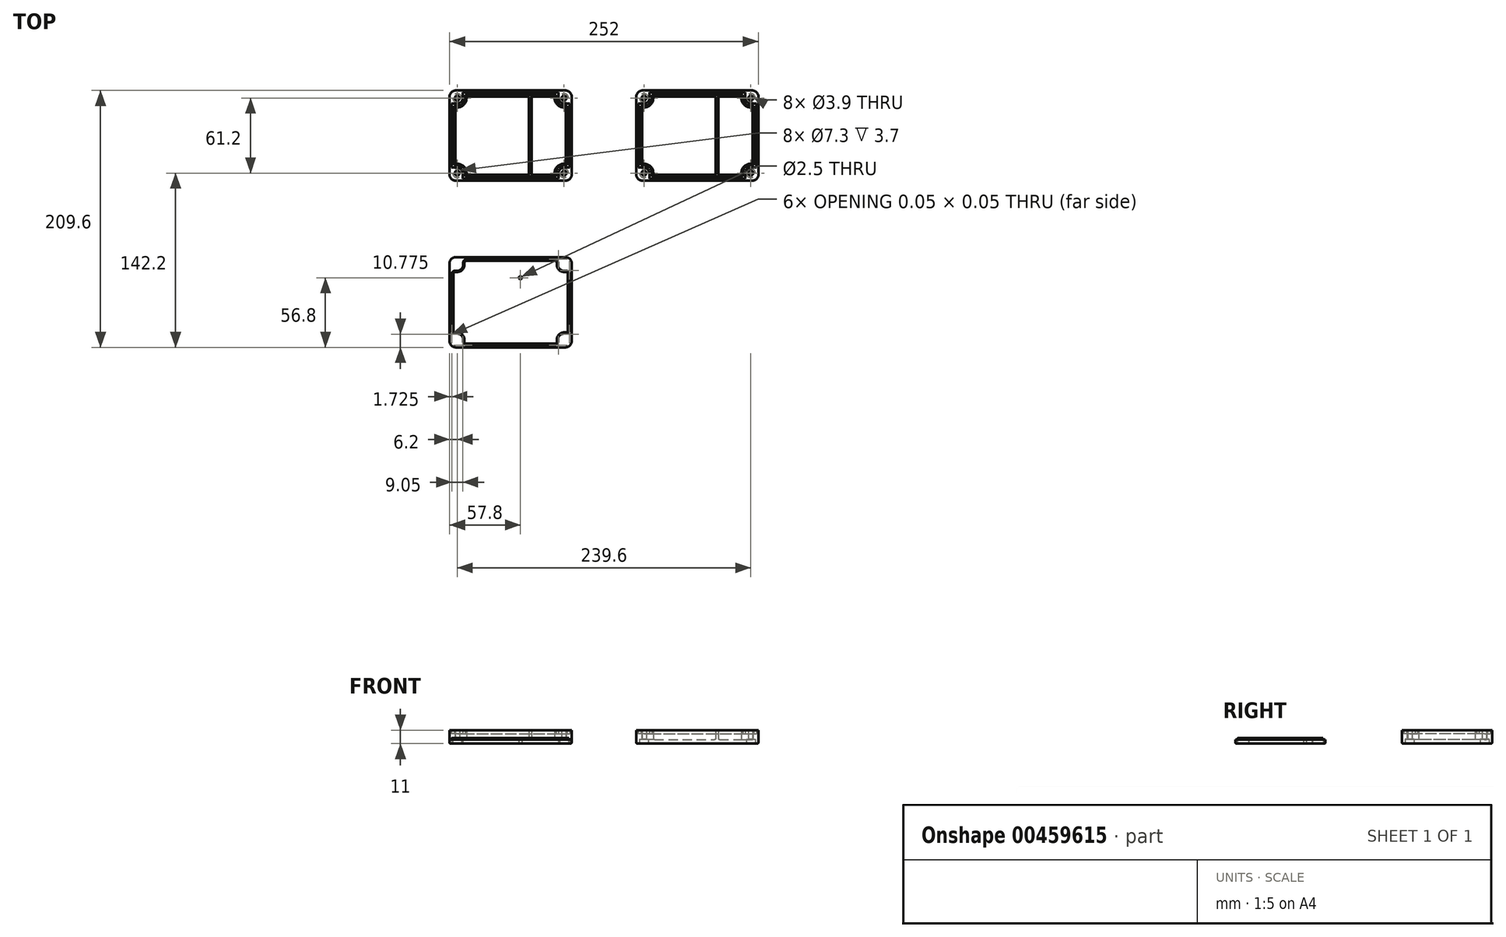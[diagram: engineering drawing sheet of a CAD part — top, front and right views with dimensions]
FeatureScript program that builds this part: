
annotation { "Feature Type Name" : "Feature", "Feature Type Description" : "" }
export const myFeature = defineFeature(function(context is Context, id is Id, definition is map)
    precondition{}
    {
        {
            var Q0;
            Q0=qCreatedBy(makeId("Top.planeOp"),FACE);
            var sketch = newSketch(context, id + "F0", { "sketchPlane" : qUnion([Q0])});
            skLineSegment(sketch, "E0.bottom", {"start": v(-25, 25) * mm, "end": v(25, 25) * mm, "construction": true});
            skLineSegment(sketch, "E0.top", {"start": v(-25, -25) * mm, "end": v(25, -25) * mm, "construction": true});
            skLineSegment(sketch, "E0.left", {"start": v(-25, 25) * mm, "end": v(-25, -25) * mm, "construction": true});
            skLineSegment(sketch, "E0.right", {"start": v(25, 25) * mm, "end": v(25, -25) * mm, "construction": true});
            skPoint(sketch, "E0.middle", {"position": v(0, 0) * mm});
            skLineSegment(sketch, "E1", {"start": v(-24, 32) * mm, "end": v(27, 32) * mm});
            skLineSegment(sketch, "E2", {"start": v(-33, 23) * mm, "end": v(-33, -23) * mm});
            skLineSegment(sketch, "E3", {"start": v(-24, -32) * mm, "end": v(27, -32) * mm});
            skLineSegment(sketch, "E4", {"start": v(28, 61.53) * mm, "end": v(28, -64.08) * mm, "construction": true});
            skLineSegment(sketch, "E5.bottom", {"start": v(31, 30) * mm, "end": v(47, 30) * mm, "construction": true});
            skLineSegment(sketch, "E5.top", {"start": v(31, -30) * mm, "end": v(47, -30) * mm, "construction": true});
            skLineSegment(sketch, "E5.left", {"start": v(31, 30) * mm, "end": v(31, -30) * mm, "construction": true});
            skLineSegment(sketch, "E5.right", {"start": v(47, 30) * mm, "end": v(47, -30) * mm, "construction": true});
            skPoint(sketch, "E5.middle", {"position": v(39, 0) * mm});
            skLineSegment(sketch, "E6", {"start": v(57, 23) * mm, "end": v(57, -23) * mm});
            skLineSegment(sketch, "E7", {"start": v(-32.8, 36.8) * mm, "end": v(56.8, 36.8) * mm});
            skLineSegment(sketch, "E8", {"start": v(-37.8, 31.8) * mm, "end": v(-37.8, -31.8) * mm});
            skLineSegment(sketch, "E9", {"start": v(-32.8, -36.8) * mm, "end": v(56.8, -36.8) * mm});
            skLineSegment(sketch, "E10", {"start": v(61.8, -31.8) * mm, "end": v(61.8, 31.8) * mm});
            skCircle(sketch, "E11", {"center": v(-31.6, 30.6) * mm, "radius": 1.95 * mm});
            skLineSegment(sketch, "E12.bottom", {"start": v(-25.1, 33.1) * mm, "end": v(49.1, 33.1) * mm});
            skLineSegment(sketch, "E12.top", {"start": v(-25.1, -33.1) * mm, "end": v(49.1, -33.1) * mm});
            skLineSegment(sketch, "E12.left", {"start": v(-34.1, 24.1) * mm, "end": v(-34.1, -24.1) * mm});
            skLineSegment(sketch, "E12.right", {"start": v(58.1, 24.1) * mm, "end": v(58.1, -24.1) * mm});
            skLineSegment(sketch, "E13.top", {"start": v(-27.1, -35.2) * mm, "end": v(51.1, -35.2) * mm});
            skLineSegment(sketch, "E13.right", {"start": v(60.2, 26.1) * mm, "end": v(60.2, -26.1) * mm});
            skLineSegment(sketch, "E14.trimOffspring", {"start": v(-27.1, 35.2) * mm, "end": v(51.1, 35.2) * mm});
            skLineSegment(sketch, "E15.trimOffspring", {"start": v(-36.2, 26.1) * mm, "end": v(-36.2, -26.1) * mm});
            skPoint(sketch, "E16.visualSharp", {"position": v(-37.8, 36.8) * mm});
            skArc(sketch, "E16.filletArc", {"start": v(-32.8, 36.8) * mm, "mid": v(-36.34, 35.34) * mm, "end": v(-37.8, 31.8) * mm});
            skLineSegment(sketch, "E17", {"start": v(27, 32) * mm, "end": v(27, -32) * mm});
            skLineSegment(sketch, "E18.MirrorCS", {"start": v(29, 32) * mm, "end": v(29, -32) * mm});
            skLineSegment(sketch, "E19.trimOffspring", {"start": v(29, 32) * mm, "end": v(48, 32) * mm});
            skLineSegment(sketch, "E20.trimOffspring", {"start": v(29, -32) * mm, "end": v(48, -32) * mm});
            skCircle(sketch, "E21", {"center": v(55.6, 30.6) * mm, "radius": 1.95 * mm});
            skArc(sketch, "E22", {"start": v(51.1, 30.6) * mm, "mid": v(52.42, 27.42) * mm, "end": v(55.6, 26.1) * mm});
            skArc(sketch, "E23", {"start": v(49.1, 30.6) * mm, "mid": v(51, 26) * mm, "end": v(55.6, 24.1) * mm});
            skArc(sketch, "E24", {"start": v(48, 30.6) * mm, "mid": v(50.23, 25.23) * mm, "end": v(55.6, 23) * mm});
            skCircle(sketch, "E25", {"center": v(55.6, -30.6) * mm, "radius": 1.95 * mm});
            skArc(sketch, "E26", {"start": v(55.6, -26.1) * mm, "mid": v(52.42, -27.42) * mm, "end": v(51.1, -30.6) * mm});
            skArc(sketch, "E27", {"start": v(55.6, -24.1) * mm, "mid": v(51, -26) * mm, "end": v(49.1, -30.6) * mm});
            skArc(sketch, "E28", {"start": v(55.6, -23) * mm, "mid": v(50.23, -25.23) * mm, "end": v(48, -30.6) * mm});
            skCircle(sketch, "E29", {"center": v(-31.6, -30.6) * mm, "radius": 1.95 * mm});
            skArc(sketch, "E30", {"start": v(-27.1, -30.6) * mm, "mid": v(-28.42, -27.42) * mm, "end": v(-31.6, -26.1) * mm});
            skArc(sketch, "E31", {"start": v(-25.1, -30.6) * mm, "mid": v(-27, -26) * mm, "end": v(-31.6, -24.1) * mm});
            skArc(sketch, "E32", {"start": v(-24, -30.6) * mm, "mid": v(-26.23, -25.23) * mm, "end": v(-31.6, -23) * mm});
            skLineSegment(sketch, "E33", {"start": v(48, 30.6) * mm, "end": v(48, 32) * mm});
            skLineSegment(sketch, "E34", {"start": v(49.1, 30.6) * mm, "end": v(49.1, 33.1) * mm});
            skLineSegment(sketch, "E35", {"start": v(51.1, 30.6) * mm, "end": v(51.1, 35.2) * mm});
            skLineSegment(sketch, "E36", {"start": v(55.6, 23) * mm, "end": v(57, 23) * mm});
            skLineSegment(sketch, "E37", {"start": v(55.6, 24.1) * mm, "end": v(58.1, 24.1) * mm});
            skLineSegment(sketch, "E38", {"start": v(55.6, 26.1) * mm, "end": v(60.2, 26.1) * mm});
            skLineSegment(sketch, "E39", {"start": v(55.6, -23) * mm, "end": v(57, -23) * mm});
            skLineSegment(sketch, "E40", {"start": v(55.6, -26.1) * mm, "end": v(60.2, -26.1) * mm});
            skLineSegment(sketch, "E41", {"start": v(48, -30.6) * mm, "end": v(48, -32) * mm});
            skLineSegment(sketch, "E42", {"start": v(49.1, -30.6) * mm, "end": v(49.1, -33.1) * mm});
            skLineSegment(sketch, "E43", {"start": v(51.1, -30.6) * mm, "end": v(51.1, -35.2) * mm});
            skLineSegment(sketch, "E44", {"start": v(55.6, -24.1) * mm, "end": v(58.1, -24.1) * mm});
            skArc(sketch, "E45", {"start": v(-31.6, 26.1) * mm, "mid": v(-28.42, 27.42) * mm, "end": v(-27.1, 30.6) * mm});
            skArc(sketch, "E46", {"start": v(-31.6, 24.1) * mm, "mid": v(-27, 26) * mm, "end": v(-25.1, 30.6) * mm});
            skArc(sketch, "E47", {"start": v(-31.6, 23) * mm, "mid": v(-26.23, 25.23) * mm, "end": v(-24, 30.6) * mm});
            skLineSegment(sketch, "E48", {"start": v(-24, 30.6) * mm, "end": v(-24, 32) * mm});
            skLineSegment(sketch, "E49", {"start": v(-25.1, 30.6) * mm, "end": v(-25.1, 33.1) * mm});
            skLineSegment(sketch, "E50", {"start": v(-27.1, 30.6) * mm, "end": v(-27.1, 35.2) * mm});
            skLineSegment(sketch, "E51", {"start": v(-31.6, 23) * mm, "end": v(-33, 23) * mm});
            skLineSegment(sketch, "E52", {"start": v(-31.6, 24.1) * mm, "end": v(-34.1, 24.1) * mm});
            skLineSegment(sketch, "E53", {"start": v(-31.6, 26.1) * mm, "end": v(-36.2, 26.1) * mm});
            skLineSegment(sketch, "E54", {"start": v(-24, -30.6) * mm, "end": v(-24, -32) * mm});
            skLineSegment(sketch, "E55", {"start": v(-25.1, -30.6) * mm, "end": v(-25.1, -33.1) * mm});
            skLineSegment(sketch, "E56", {"start": v(-27.1, -30.6) * mm, "end": v(-27.1, -35.2) * mm});
            skLineSegment(sketch, "E57", {"start": v(-31.6, -23) * mm, "end": v(-33, -23) * mm});
            skLineSegment(sketch, "E58", {"start": v(-31.6, -24.1) * mm, "end": v(-34.1, -24.1) * mm});
            skLineSegment(sketch, "E59", {"start": v(-31.6, -26.1) * mm, "end": v(-36.2, -26.1) * mm});
            skPoint(sketch, "E60.visualSharp", {"position": v(61.8, 36.8) * mm});
            skArc(sketch, "E60.filletArc", {"start": v(61.8, 31.8) * mm, "mid": v(60.34, 35.34) * mm, "end": v(56.8, 36.8) * mm});
            skPoint(sketch, "E61.visualSharp", {"position": v(61.8, -36.8) * mm});
            skArc(sketch, "E61.filletArc", {"start": v(56.8, -36.8) * mm, "mid": v(60.34, -35.34) * mm, "end": v(61.8, -31.8) * mm});
            skPoint(sketch, "E62.visualSharp", {"position": v(-37.8, -36.8) * mm});
            skArc(sketch, "E62.filletArc", {"start": v(-37.8, -31.8) * mm, "mid": v(-36.34, -35.34) * mm, "end": v(-32.8, -36.8) * mm});
            skSolve(sketch);
        }
        {
            var Q0;
            Q0=makeQuery(id+"F0.imprint","IMPRINT",FACE,{"disambiguationData":[TD([[makeQuery(id+"F0.imprint","IMPRINT",EDGE,{"derivedFrom":sQuery(id+"F0.wireOp",EDGE,"E7")}),-1.0]])]});
            var Q1;
            Q1=makeQuery(id+"F0.imprint","IMPRINT",FACE,{"disambiguationData":[TD([[makeQuery(id+"F0.imprint","IMPRINT",EDGE,{"derivedFrom":sQuery(id+"F0.wireOp",EDGE,"E1")}),1.0]])]});
            extrude(context, id + "F1", {"entities" : qUnion([Q0, Q1]), "depth" : 11 * mm});
        }
        {
            var Q0;
            Q0=makeQuery(id+"F0.imprint","IMPRINT",FACE,{"disambiguationData":[TD([[makeQuery(id+"F0.imprint","IMPRINT",EDGE,{"derivedFrom":sQuery(id+"F0.wireOp",EDGE,"E12.bottom")}),1.0]])]});
            extrude(context, id + "F2", {"entities" : qUnion([Q0]), "operationType" : NewBodyOperationType.ADD, "depth" : 8 * mm});
        }
        {
            var Q0;
            Q0=makeQuery(id+"F0.imprint","IMPRINT",FACE,{"disambiguationData":[TD([[makeQuery(id+"F0.imprint","IMPRINT",EDGE,{"derivedFrom":sQuery(id+"F0.wireOp",EDGE,"E6")}),-1.0]])]});
            var Q1;
            Q1=makeQuery(id+"F0.imprint","IMPRINT",FACE,{"disambiguationData":[TD([[makeQuery(id+"F0.imprint","IMPRINT",EDGE,{"derivedFrom":sQuery(id+"F0.wireOp",EDGE,"E1")}),-1.0]])]});
            extrude(context, id + "F3", {"entities" : qUnion([Q0, Q1]), "operationType" : NewBodyOperationType.ADD, "depth" : 3.2 * mm});
        }
        {
            var Q0;
            Q0=qCreatedBy(makeId("Top.planeOp"),FACE);
            var sketch = newSketch(context, id + "F4", { "sketchPlane" : qUnion([Q0])});
            skLineSegment(sketch, "E63", {"start": v(0, 0) * mm, "end": v(0, -187.5) * mm, "construction": true});
            skLineSegment(sketch, "E64", {"start": v(0, -136) * mm, "end": v(-72.43, -136) * mm, "construction": true});
            skLineSegment(sketch, "E65", {"start": v(0, -136) * mm, "end": v(90.36, -136) * mm, "construction": true});
            skLineSegment(sketch, "E66.bottom", {"start": v(-25, -111) * mm, "end": v(25, -111) * mm, "construction": true});
            skLineSegment(sketch, "E66.top", {"start": v(-25, -161) * mm, "end": v(25, -161) * mm, "construction": true});
            skLineSegment(sketch, "E66.left", {"start": v(-25, -111) * mm, "end": v(-25, -161) * mm, "construction": true});
            skLineSegment(sketch, "E66.right", {"start": v(25, -111) * mm, "end": v(25, -161) * mm, "construction": true});
            skPoint(sketch, "E66.middle", {"position": v(0, -136) * mm});
            skLineSegment(sketch, "E67.bottom", {"start": v(31, -106) * mm, "end": v(47, -106) * mm, "construction": true});
            skLineSegment(sketch, "E67.top", {"start": v(31, -166) * mm, "end": v(47, -166) * mm, "construction": true});
            skLineSegment(sketch, "E67.left", {"start": v(31, -106) * mm, "end": v(31, -166) * mm, "construction": true});
            skLineSegment(sketch, "E67.right", {"start": v(47, -106) * mm, "end": v(47, -166) * mm, "construction": true});
            skPoint(sketch, "E67.middle", {"position": v(39, -136) * mm});
            skLineSegment(sketch, "E68", {"start": v(28, -80.22) * mm, "end": v(28, -200.99) * mm, "construction": true});
            skLineSegment(sketch, "E69", {"start": v(-25.2, -102.8) * mm, "end": v(49.2, -102.8) * mm});
            skLineSegment(sketch, "E70", {"start": v(58.2, -111.8) * mm, "end": v(58.2, -160.2) * mm});
            skLineSegment(sketch, "E71", {"start": v(49.2, -169.2) * mm, "end": v(-25.2, -169.2) * mm});
            skLineSegment(sketch, "E72", {"start": v(-34.2, -160.2) * mm, "end": v(-34.2, -111.8) * mm});
            skLineSegment(sketch, "E73", {"start": v(-32.8, -99.2) * mm, "end": v(56.8, -99.2) * mm});
            skLineSegment(sketch, "E74", {"start": v(61.8, -104.2) * mm, "end": v(61.8, -167.8) * mm});
            skLineSegment(sketch, "E75", {"start": v(56.8, -172.8) * mm, "end": v(-32.8, -172.8) * mm});
            skLineSegment(sketch, "E76", {"start": v(-37.8, -167.8) * mm, "end": v(-37.8, -104.2) * mm});
            skLineSegment(sketch, "E77", {"start": v(-27, -100.9) * mm, "end": v(51.05, -100.9) * mm});
            skLineSegment(sketch, "E78", {"start": v(60.1, -109.95) * mm, "end": v(60.1, -162.05) * mm});
            skLineSegment(sketch, "E79", {"start": v(51.05, -171.1) * mm, "end": v(-27.05, -171.1) * mm});
            skLineSegment(sketch, "E80", {"start": v(-36.1, -162.05) * mm, "end": v(-36.1, -110) * mm});
            skCircle(sketch, "E81", {"center": v(-31.6, -105.4) * mm, "radius": 1.25 * mm});
            skCircle(sketch, "E82", {"center": v(55.6, -105.4) * mm, "radius": 1.25 * mm});
            skCircle(sketch, "E83", {"center": v(55.6, -166.6) * mm, "radius": 1.25 * mm});
            skCircle(sketch, "E84", {"center": v(-31.6, -166.6) * mm, "radius": 1.25 * mm});
            skArc(sketch, "E85", {"start": v(-31.6, -110) * mm, "mid": v(-28.35, -108.65) * mm, "end": v(-27, -105.4) * mm});
            skArc(sketch, "E86", {"start": v(-31.6, -111.8) * mm, "mid": v(-27.07, -109.93) * mm, "end": v(-25.2, -105.4) * mm});
            skLineSegment(sketch, "E87", {"start": v(-25.2, -105.4) * mm, "end": v(-25.2, -102.8) * mm});
            skLineSegment(sketch, "E88", {"start": v(-31.6, -111.8) * mm, "end": v(-34.2, -111.8) * mm});
            skLineSegment(sketch, "E89", {"start": v(-31.6, -110) * mm, "end": v(-36.1, -110) * mm});
            skLineSegment(sketch, "E90", {"start": v(-27, -105.4) * mm, "end": v(-27, -100.9) * mm});
            skArc(sketch, "E91", {"start": v(51, -105.4) * mm, "mid": v(52.35, -108.65) * mm, "end": v(55.6, -110) * mm});
            skArc(sketch, "E92", {"start": v(49.2, -105.4) * mm, "mid": v(51.07, -109.93) * mm, "end": v(55.6, -111.8) * mm});
            skArc(sketch, "E93", {"start": v(-27, -166.6) * mm, "mid": v(-28.35, -163.35) * mm, "end": v(-31.6, -162) * mm});
            skArc(sketch, "E94", {"start": v(-36.05, -162) * mm, "mid": v(-36.07, -162.02) * mm, "end": v(-36.1, -162.05) * mm});
            skArc(sketch, "E95", {"start": v(55.6, -162) * mm, "mid": v(52.35, -163.35) * mm, "end": v(51, -166.6) * mm});
            skArc(sketch, "E96", {"start": v(51, -171.05) * mm, "mid": v(51.02, -171.07) * mm, "end": v(51.05, -171.1) * mm});
            skLineSegment(sketch, "E97", {"start": v(49.2, -105.4) * mm, "end": v(49.2, -102.8) * mm});
            skLineSegment(sketch, "E98", {"start": v(51, -105.4) * mm, "end": v(51, -100.9) * mm});
            skLineSegment(sketch, "E99", {"start": v(55.6, -111.8) * mm, "end": v(58.2, -111.8) * mm});
            skLineSegment(sketch, "E100", {"start": v(55.6, -110) * mm, "end": v(60.1, -110) * mm});
            skLineSegment(sketch, "E101", {"start": v(55.6, -160.2) * mm, "end": v(58.2, -160.2) * mm});
            skLineSegment(sketch, "E102", {"start": v(55.6, -162) * mm, "end": v(60.1, -162) * mm});
            skLineSegment(sketch, "E103", {"start": v(49.2, -166.6) * mm, "end": v(49.2, -169.2) * mm});
            skLineSegment(sketch, "E104", {"start": v(51, -166.6) * mm, "end": v(51, -171.1) * mm});
            skLineSegment(sketch, "E105", {"start": v(-31.6, -160.2) * mm, "end": v(-34.2, -160.2) * mm});
            skLineSegment(sketch, "E106", {"start": v(-36.1, -162) * mm, "end": v(-31.6, -162) * mm});
            skLineSegment(sketch, "E107", {"start": v(-25.2, -166.6) * mm, "end": v(-25.2, -169.2) * mm});
            skLineSegment(sketch, "E108", {"start": v(-27, -166.6) * mm, "end": v(-27, -171.1) * mm});
            skArc(sketch, "E109.trimOffspring", {"start": v(51.05, -100.9) * mm, "mid": v(51.02, -100.93) * mm, "end": v(51, -100.95) * mm});
            skArc(sketch, "E110.trimOffspring", {"start": v(60.05, -110) * mm, "mid": v(60.07, -109.98) * mm, "end": v(60.1, -109.95) * mm});
            skArc(sketch, "E111.trimOffspring", {"start": v(60.1, -162.05) * mm, "mid": v(60.07, -162.02) * mm, "end": v(60.05, -162) * mm});
            skArc(sketch, "E112.trimOffspring", {"start": v(55.6, -160.2) * mm, "mid": v(51.07, -162.07) * mm, "end": v(49.2, -166.6) * mm});
            skArc(sketch, "E113.trimOffspring", {"start": v(-27.05, -171.1) * mm, "mid": v(-27.02, -171.07) * mm, "end": v(-27, -171.05) * mm});
            skArc(sketch, "E114.trimOffspring", {"start": v(-25.2, -166.6) * mm, "mid": v(-27.07, -162.07) * mm, "end": v(-31.6, -160.2) * mm});
            skCircle(sketch, "E115", {"center": v(-20, -116) * mm, "radius": 1.25 * mm});
            skCircle(sketch, "E116", {"center": v(-20, -116) * mm, "radius": 2.75 * mm});
            skCircle(sketch, "E117.MirrorC", {"center": v(20, -116) * mm, "radius": 2.75 * mm});
            skCircle(sketch, "E118.MirrorC", {"center": v(20, -116) * mm, "radius": 1.25 * mm});
            skCircle(sketch, "E119.MirrorC", {"center": v(-20, -156) * mm, "radius": 1.25 * mm});
            skCircle(sketch, "E120.MirrorC", {"center": v(-20, -156) * mm, "radius": 2.75 * mm});
            skCircle(sketch, "E121.MirrorC", {"center": v(20, -156) * mm, "radius": 1.25 * mm});
            skCircle(sketch, "E122.MirrorC", {"center": v(20, -156) * mm, "radius": 2.75 * mm});
            skPoint(sketch, "E123.visualSharp", {"position": v(-37.8, -99.2) * mm});
            skArc(sketch, "E123.filletArc", {"start": v(-32.8, -99.2) * mm, "mid": v(-36.34, -100.66) * mm, "end": v(-37.8, -104.2) * mm});
            skPoint(sketch, "E124.visualSharp", {"position": v(61.8, -99.2) * mm});
            skArc(sketch, "E124.filletArc", {"start": v(61.8, -104.2) * mm, "mid": v(60.34, -100.66) * mm, "end": v(56.8, -99.2) * mm});
            skPoint(sketch, "E125.visualSharp", {"position": v(61.8, -172.8) * mm});
            skArc(sketch, "E125.filletArc", {"start": v(56.8, -172.8) * mm, "mid": v(60.34, -171.34) * mm, "end": v(61.8, -167.8) * mm});
            skPoint(sketch, "E126.visualSharp", {"position": v(-37.8, -172.8) * mm});
            skArc(sketch, "E126.filletArc", {"start": v(-37.8, -167.8) * mm, "mid": v(-36.34, -171.34) * mm, "end": v(-32.8, -172.8) * mm});
            skLineSegment(sketch, "E127", {"start": v(27, -102.8) * mm, "end": v(27, -169.2) * mm});
            skLineSegment(sketch, "E128", {"start": v(29, -102.8) * mm, "end": v(29, -169.2) * mm});
            skSolve(sketch);
        }
        {
            var Q0;
            Q0=makeQuery(id+"F4.imprint","IMPRINT",FACE,{"disambiguationData":[TD([[makeQuery(id+"F4.imprint","IMPRINT",EDGE,{"derivedFrom":sQuery(id+"F4.wireOp",EDGE,"E73")}),-1.0]])]});
            var Q1;
            {var subQ0=sQuery(id+"F4.wireOp",EDGE,"E127");Q1=makeQuery(id+"F4.imprint","IMPRINT",FACE,{"disambiguationData":[TD([[makeQuery(id+"F4.imprint","IMPRINT",EDGE,{"derivedFrom":subQ0}),1.0]])]});}
            extrude(context, id + "F5", {"entities" : qUnion([Q0, Q1]), "depth" : 3.2 * mm});
        }
        {
            var Q0;
            Q0=makeQuery(id+"F4.imprint","IMPRINT",FACE,{"disambiguationData":[TD([[makeQuery(id+"F4.imprint","IMPRINT",EDGE,{"derivedFrom":sQuery(id+"F4.wireOp",EDGE,"E70")}),1.0]])]});
            extrude(context, id + "F6", {"entities" : qUnion([Q0]), "operationType" : NewBodyOperationType.ADD, "depth" : 4.7 * mm});
        }
        {
            var Q0;
            Q0=makeQuery(id+"F4.imprint","IMPRINT",FACE,{"disambiguationData":[TD([[makeQuery(id+"F4.imprint","IMPRINT",EDGE,{"derivedFrom":sQuery(id+"F4.wireOp",EDGE,"E81")}),1.0]])]});
            var Q1;
            Q1=makeQuery(id+"F4.imprint","IMPRINT",FACE,{"disambiguationData":[TD([[makeQuery(id+"F4.imprint","IMPRINT",EDGE,{"derivedFrom":sQuery(id+"F4.wireOp",EDGE,"E82")}),1.0]])]});
            var Q2;
            Q2=makeQuery(id+"F4.imprint","IMPRINT",FACE,{"disambiguationData":[TD([[makeQuery(id+"F4.imprint","IMPRINT",EDGE,{"derivedFrom":sQuery(id+"F4.wireOp",EDGE,"E84")}),1.0]])]});
            var Q3;
            Q3=makeQuery(id+"F4.imprint","IMPRINT",FACE,{"disambiguationData":[TD([[makeQuery(id+"F4.imprint","IMPRINT",EDGE,{"derivedFrom":sQuery(id+"F4.wireOp",EDGE,"E83")}),1.0]])]});
            var Q4;
            Q4=makeQuery(id+"F4.imprint","IMPRINT",FACE,{"disambiguationData":[TD([[makeQuery(id+"F4.imprint","IMPRINT",EDGE,{"derivedFrom":sQuery(id+"F4.wireOp",EDGE,"E70")}),-1.0]])]});
            var Q5;
            Q5=makeQuery(id+"F4.imprint","IMPRINT",FACE,{"disambiguationData":[TD([[makeQuery(id+"F4.imprint","IMPRINT",EDGE,{"derivedFrom":sQuery(id+"F4.wireOp",EDGE,"E72")}),-1.0]])]});
            extrude(context, id + "F7", {"entities" : qUnion([Q0, Q1, Q2, Q3, Q4, Q5]), "operationType" : NewBodyOperationType.ADD, "depth" : 3.2 * mm});
        }
        {
            var Q0;
            Q0=makeQuery(id+"F4.imprint","IMPRINT",FACE,{"disambiguationData":[TD([[makeQuery(id+"F4.imprint","IMPRINT",EDGE,{"derivedFrom":sQuery(id+"F4.wireOp",EDGE,"E115")}),-1.0]])]});
            var Q1;
            Q1=makeQuery(id+"F4.imprint","IMPRINT",FACE,{"disambiguationData":[TD([[makeQuery(id+"F4.imprint","IMPRINT",EDGE,{"derivedFrom":sQuery(id+"F4.wireOp",EDGE,"E119.MirrorC")}),1.0]])]});
            var Q2;
            Q2=makeQuery(id+"F4.imprint","IMPRINT",FACE,{"disambiguationData":[TD([[makeQuery(id+"F4.imprint","IMPRINT",EDGE,{"derivedFrom":sQuery(id+"F4.wireOp",EDGE,"E121.MirrorC")}),-1.0]])]});
            var Q3;
            Q3=makeQuery(id+"F4.imprint","IMPRINT",FACE,{"disambiguationData":[TD([[makeQuery(id+"F4.imprint","IMPRINT",EDGE,{"derivedFrom":sQuery(id+"F4.wireOp",EDGE,"E117.MirrorC")}),-1.0]])]});
            var Q4;
            {var subQ0=sQuery(id+"F4.wireOp",EDGE,"E128");var subQ1=sQuery(id+"F4.wireOp",EDGE,"E71");var subQ2=sQuery(id+"F4.wireOp",EDGE,"E69");var subQ3=sQuery(id+"F4.wireOp",EDGE,"E127");Q4=makeQuery(id+"F7.boolean.opBoolean","MERGE",FACE,{"derivedFrom":[makeQuery(id+"F5.opExtrude","CAP_FACE",FACE,{"disambiguationData":[OSD([subQ2,subQ1,subQ3,subQ0])],"isStart":false}),makeQuery(id+"F7.opExtrude","CAP_FACE",FACE,{"disambiguationData":[OSD([subQ2,subQ1,sQuery(id+"F4.wireOp",EDGE,"E72"),sQuery(id+"F4.wireOp",EDGE,"E86"),sQuery(id+"F4.wireOp",EDGE,"E87"),sQuery(id+"F4.wireOp",EDGE,"E88"),sQuery(id+"F4.wireOp",EDGE,"E105"),sQuery(id+"F4.wireOp",EDGE,"E107"),sQuery(id+"F4.wireOp",EDGE,"E114.trimOffspring"),sQuery(id+"F4.wireOp",EDGE,"E116"),sQuery(id+"F4.wireOp",EDGE,"E117.MirrorC"),sQuery(id+"F4.wireOp",EDGE,"E120.MirrorC"),sQuery(id+"F4.wireOp",EDGE,"E122.MirrorC"),subQ3])],"isStart":false}),makeQuery(id+"F7.opExtrude","CAP_FACE",FACE,{"disambiguationData":[OSD([subQ2,sQuery(id+"F4.wireOp",EDGE,"E70"),subQ1,sQuery(id+"F4.wireOp",EDGE,"E92"),sQuery(id+"F4.wireOp",EDGE,"E97"),sQuery(id+"F4.wireOp",EDGE,"E99"),sQuery(id+"F4.wireOp",EDGE,"E101"),sQuery(id+"F4.wireOp",EDGE,"E103"),sQuery(id+"F4.wireOp",EDGE,"E112.trimOffspring"),subQ0])],"isStart":false})]});}
            extrude(context, id + "F8", {"entities" : qUnion([Q0, Q1, Q2, Q3]), "operationType" : NewBodyOperationType.ADD, "endBound" : BoundingType.UP_TO_SURFACE, "endBoundEntityFace" : qUnion([Q4]), "depth" : 13.2 * mm});
        }
        {
            var Q0;
            Q0=makeQuery(id+"F4.imprint","IMPRINT",FACE,{"disambiguationData":[TD([[makeQuery(id+"F4.imprint","IMPRINT",EDGE,{"derivedFrom":sQuery(id+"F4.wireOp",EDGE,"E115")}),1.0]])]});
            var Q1;
            Q1=makeQuery(id+"F4.imprint","IMPRINT",FACE,{"disambiguationData":[TD([[makeQuery(id+"F4.imprint","IMPRINT",EDGE,{"derivedFrom":sQuery(id+"F4.wireOp",EDGE,"E118.MirrorC")}),-1.0]])]});
            var Q2;
            Q2=makeQuery(id+"F4.imprint","IMPRINT",FACE,{"disambiguationData":[TD([[makeQuery(id+"F4.imprint","IMPRINT",EDGE,{"derivedFrom":sQuery(id+"F4.wireOp",EDGE,"E121.MirrorC")}),1.0]])]});
            var Q3;
            Q3=makeQuery(id+"F4.imprint","IMPRINT",FACE,{"disambiguationData":[TD([[makeQuery(id+"F4.imprint","IMPRINT",EDGE,{"derivedFrom":sQuery(id+"F4.wireOp",EDGE,"E119.MirrorC")}),-1.0]])]});
            var Q4;
            Q4=makeQuery(id+"F7.opExtrude","CAP_FACE",FACE,{"disambiguationData":[OSD([sQuery(id+"F4.wireOp",EDGE,"E69"),sQuery(id+"F4.wireOp",EDGE,"E71"),sQuery(id+"F4.wireOp",EDGE,"E72"),sQuery(id+"F4.wireOp",EDGE,"E86"),sQuery(id+"F4.wireOp",EDGE,"E87"),sQuery(id+"F4.wireOp",EDGE,"E88"),sQuery(id+"F4.wireOp",EDGE,"E105"),sQuery(id+"F4.wireOp",EDGE,"E107"),sQuery(id+"F4.wireOp",EDGE,"E114.trimOffspring"),sQuery(id+"F4.wireOp",EDGE,"E116"),sQuery(id+"F4.wireOp",EDGE,"E117.MirrorC"),sQuery(id+"F4.wireOp",EDGE,"E120.MirrorC"),sQuery(id+"F4.wireOp",EDGE,"E122.MirrorC"),sQuery(id+"F4.wireOp",EDGE,"E127")])],"isStart":false});
            extrude(context, id + "F9", {"entities" : qUnion([Q0, Q1, Q2, Q3]), "operationType" : NewBodyOperationType.ADD, "endBound" : BoundingType.UP_TO_SURFACE, "endBoundEntityFace" : qUnion([Q4]), "depth" : 25 * mm});
        }
        {
            var Q0;
            Q0=makeQuery(id+"F5.opExtrude","SWEPT_EDGE",EDGE,{"disambiguationData":[OSD([sQuery(id+"F4.wireOp",EDGE,"E69"),sQuery(id+"F4.wireOp",EDGE,"E127")])]});
            var Q1;
            Q1=makeQuery(id+"F6.opExtrude","SWEPT_EDGE",EDGE,{"disambiguationData":[OSD([sQuery(id+"F4.wireOp",EDGE,"E69"),sQuery(id+"F4.wireOp",EDGE,"E97")])]});
            var Q2;
            Q2=makeQuery(id+"F6.opExtrude","SWEPT_EDGE",EDGE,{"disambiguationData":[OSD([sQuery(id+"F4.wireOp",EDGE,"E70"),sQuery(id+"F4.wireOp",EDGE,"E99")])]});
            var Q3;
            Q3=makeQuery(id+"F6.opExtrude","SWEPT_EDGE",EDGE,{"disambiguationData":[OSD([sQuery(id+"F4.wireOp",EDGE,"E70"),sQuery(id+"F4.wireOp",EDGE,"E101")])]});
            var Q4;
            Q4=makeQuery(id+"F6.opExtrude","SWEPT_EDGE",EDGE,{"disambiguationData":[OSD([sQuery(id+"F4.wireOp",EDGE,"E71"),sQuery(id+"F4.wireOp",EDGE,"E103")])]});
            var Q5;
            Q5=makeQuery(id+"F5.opExtrude","SWEPT_EDGE",EDGE,{"disambiguationData":[OSD([sQuery(id+"F4.wireOp",EDGE,"E71"),sQuery(id+"F4.wireOp",EDGE,"E128")])]});
            var Q6;
            Q6=makeQuery(id+"F5.opExtrude","SWEPT_EDGE",EDGE,{"disambiguationData":[OSD([sQuery(id+"F4.wireOp",EDGE,"E69"),sQuery(id+"F4.wireOp",EDGE,"E128")])]});
            var Q7;
            Q7=makeQuery(id+"F5.opExtrude","SWEPT_EDGE",EDGE,{"disambiguationData":[OSD([sQuery(id+"F4.wireOp",EDGE,"E71"),sQuery(id+"F4.wireOp",EDGE,"E127")])]});
            var Q8;
            Q8=makeQuery(id+"F6.opExtrude","SWEPT_EDGE",EDGE,{"disambiguationData":[OSD([sQuery(id+"F4.wireOp",EDGE,"E69"),sQuery(id+"F4.wireOp",EDGE,"E87")])]});
            var Q9;
            Q9=makeQuery(id+"F6.opExtrude","SWEPT_EDGE",EDGE,{"disambiguationData":[OSD([sQuery(id+"F4.wireOp",EDGE,"E72"),sQuery(id+"F4.wireOp",EDGE,"E88")])]});
            var Q10;
            Q10=makeQuery(id+"F6.opExtrude","SWEPT_EDGE",EDGE,{"disambiguationData":[OSD([sQuery(id+"F4.wireOp",EDGE,"E71"),sQuery(id+"F4.wireOp",EDGE,"E107")])]});
            var Q11;
            Q11=makeQuery(id+"F6.opExtrude","SWEPT_EDGE",EDGE,{"disambiguationData":[OSD([sQuery(id+"F4.wireOp",EDGE,"E72"),sQuery(id+"F4.wireOp",EDGE,"E105")])]});
            fillet(context, id + "F10", {"entities" : qUnion([Q0, Q1, Q2, Q3, Q4, Q5, Q6, Q7, Q8, Q9, Q10, Q11]), "radius" : 1 * mm, "tangentPropagation" : true, "allowEdgeOverflow" : false});
        }
        {
            var Q0;
            Q0=makeQuery(id+"F1.opExtrude","SWEPT_EDGE",EDGE,{"disambiguationData":[OSD([sQuery(id+"F0.wireOp",EDGE,"E2"),sQuery(id+"F0.wireOp",EDGE,"E57")])]});
            var Q1;
            Q1=makeQuery(id+"F1.opExtrude","SWEPT_EDGE",EDGE,{"disambiguationData":[OSD([sQuery(id+"F0.wireOp",EDGE,"E3"),sQuery(id+"F0.wireOp",EDGE,"E54")])]});
            var Q2;
            Q2=makeQuery(id+"F1.opExtrude","SWEPT_EDGE",EDGE,{"disambiguationData":[OSD([sQuery(id+"F0.wireOp",EDGE,"E2"),sQuery(id+"F0.wireOp",EDGE,"E51")])]});
            var Q3;
            Q3=makeQuery(id+"F1.opExtrude","SWEPT_EDGE",EDGE,{"disambiguationData":[OSD([sQuery(id+"F0.wireOp",EDGE,"E1"),sQuery(id+"F0.wireOp",EDGE,"E48")])]});
            var Q4;
            Q4=makeQuery(id+"F1.opExtrude","SWEPT_EDGE",EDGE,{"disambiguationData":[OSD([sQuery(id+"F0.wireOp",EDGE,"E3"),sQuery(id+"F0.wireOp",EDGE,"E17")])]});
            var Q5;
            Q5=makeQuery(id+"F1.opExtrude","SWEPT_EDGE",EDGE,{"disambiguationData":[OSD([sQuery(id+"F0.wireOp",EDGE,"E1"),sQuery(id+"F0.wireOp",EDGE,"E17")])]});
            var Q6;
            Q6=makeQuery(id+"F1.opExtrude","SWEPT_EDGE",EDGE,{"disambiguationData":[OSD([sQuery(id+"F0.wireOp",EDGE,"E20.trimOffspring"),sQuery(id+"F0.wireOp",EDGE,"E41")])]});
            var Q7;
            Q7=makeQuery(id+"F1.opExtrude","SWEPT_EDGE",EDGE,{"disambiguationData":[OSD([sQuery(id+"F0.wireOp",EDGE,"E6"),sQuery(id+"F0.wireOp",EDGE,"E39")])]});
            var Q8;
            Q8=makeQuery(id+"F1.opExtrude","SWEPT_EDGE",EDGE,{"disambiguationData":[OSD([sQuery(id+"F0.wireOp",EDGE,"E18.MirrorCS"),sQuery(id+"F0.wireOp",EDGE,"E20.trimOffspring")])]});
            var Q9;
            Q9=makeQuery(id+"F1.opExtrude","SWEPT_EDGE",EDGE,{"disambiguationData":[OSD([sQuery(id+"F0.wireOp",EDGE,"E6"),sQuery(id+"F0.wireOp",EDGE,"E36")])]});
            var Q10;
            Q10=makeQuery(id+"F1.opExtrude","SWEPT_EDGE",EDGE,{"disambiguationData":[OSD([sQuery(id+"F0.wireOp",EDGE,"E19.trimOffspring"),sQuery(id+"F0.wireOp",EDGE,"E33")])]});
            var Q11;
            Q11=makeQuery(id+"F1.opExtrude","SWEPT_EDGE",EDGE,{"disambiguationData":[OSD([sQuery(id+"F0.wireOp",EDGE,"E18.MirrorCS"),sQuery(id+"F0.wireOp",EDGE,"E19.trimOffspring")])]});
            fillet(context, id + "F11", {"entities" : qUnion([Q0, Q1, Q2, Q3, Q4, Q5, Q6, Q7, Q8, Q9, Q10, Q11]), "radius" : 1 * mm, "tangentPropagation" : true, "allowEdgeOverflow" : false});
        }
        {
            var Q0;
            {var subQ0=sQuery(id+"F0.wireOp",EDGE,"E41");var subQ1=sQuery(id+"F0.wireOp",EDGE,"E39");var subQ2=sQuery(id+"F0.wireOp",EDGE,"E36");var subQ3=sQuery(id+"F0.wireOp",EDGE,"E33");var subQ4=sQuery(id+"F0.wireOp",EDGE,"E28");var subQ5=sQuery(id+"F0.wireOp",EDGE,"E24");var subQ6=sQuery(id+"F0.wireOp",EDGE,"E20.trimOffspring");var subQ7=sQuery(id+"F0.wireOp",EDGE,"E19.trimOffspring");var subQ8=sQuery(id+"F0.wireOp",EDGE,"E18.MirrorCS");var subQ9=sQuery(id+"F0.wireOp",EDGE,"E6");var subQ10=sQuery(id+"F0.wireOp",EDGE,"E57");var subQ11=sQuery(id+"F0.wireOp",EDGE,"E54");var subQ12=sQuery(id+"F0.wireOp",EDGE,"E51");var subQ13=sQuery(id+"F0.wireOp",EDGE,"E48");var subQ14=sQuery(id+"F0.wireOp",EDGE,"E47");var subQ15=sQuery(id+"F0.wireOp",EDGE,"E32");var subQ16=sQuery(id+"F0.wireOp",EDGE,"E17");var subQ17=sQuery(id+"F0.wireOp",EDGE,"E3");var subQ18=sQuery(id+"F0.wireOp",EDGE,"E2");var subQ19=sQuery(id+"F0.wireOp",EDGE,"E1");var subQ20=sQuery(id+"F0.wireOp",EDGE,"E59");var subQ21=sQuery(id+"F0.wireOp",EDGE,"E58");var subQ22=sQuery(id+"F0.wireOp",EDGE,"E56");var subQ23=sQuery(id+"F0.wireOp",EDGE,"E55");var subQ24=sQuery(id+"F0.wireOp",EDGE,"E53");var subQ25=sQuery(id+"F0.wireOp",EDGE,"E52");var subQ26=sQuery(id+"F0.wireOp",EDGE,"E50");var subQ27=sQuery(id+"F0.wireOp",EDGE,"E49");var subQ28=sQuery(id+"F0.wireOp",EDGE,"E46");var subQ29=sQuery(id+"F0.wireOp",EDGE,"E45");var subQ30=sQuery(id+"F0.wireOp",EDGE,"E44");var subQ31=sQuery(id+"F0.wireOp",EDGE,"E43");var subQ32=sQuery(id+"F0.wireOp",EDGE,"E42");var subQ33=sQuery(id+"F0.wireOp",EDGE,"E40");var subQ34=sQuery(id+"F0.wireOp",EDGE,"E38");var subQ35=sQuery(id+"F0.wireOp",EDGE,"E37");var subQ36=sQuery(id+"F0.wireOp",EDGE,"E35");var subQ37=sQuery(id+"F0.wireOp",EDGE,"E34");var subQ38=sQuery(id+"F0.wireOp",EDGE,"E31");var subQ39=sQuery(id+"F0.wireOp",EDGE,"E30");var subQ40=sQuery(id+"F0.wireOp",EDGE,"E27");var subQ41=sQuery(id+"F0.wireOp",EDGE,"E26");var subQ42=sQuery(id+"F0.wireOp",EDGE,"E23");var subQ43=sQuery(id+"F0.wireOp",EDGE,"E22");var subQ44=sQuery(id+"F0.wireOp",EDGE,"E15.trimOffspring");var subQ45=sQuery(id+"F0.wireOp",EDGE,"E14.trimOffspring");var subQ46=sQuery(id+"F0.wireOp",EDGE,"E13.right");var subQ47=sQuery(id+"F0.wireOp",EDGE,"E13.top");var subQ48=sQuery(id+"F0.wireOp",EDGE,"E12.right");var subQ49=sQuery(id+"F0.wireOp",EDGE,"E12.left");var subQ50=sQuery(id+"F0.wireOp",EDGE,"E12.top");var subQ51=sQuery(id+"F0.wireOp",EDGE,"E12.bottom");Q0=makeQuery(id+"F3.boolean.opBoolean","MERGE",FACE,{"derivedFrom":[makeQuery(id+"F2.boolean.opBoolean","MERGE",FACE,{"derivedFrom":[makeQuery(id+"F1.opExtrude","CAP_FACE",FACE,{"disambiguationData":[OSD([subQ19,subQ18,subQ17,subQ9,subQ51,subQ50,subQ49,subQ48,subQ16,subQ8,subQ7,subQ6,subQ42,subQ5,subQ40,subQ4,subQ38,subQ15,subQ3,subQ37,subQ2,subQ35,subQ1,subQ0,subQ32,subQ30,subQ28,subQ14,subQ13,subQ27,subQ12,subQ25,subQ11,subQ23,subQ10,subQ21])],"isStart":true}),makeQuery(id+"F1.opExtrude","CAP_FACE",FACE,{"disambiguationData":[OSD([sQuery(id+"F0.wireOp",EDGE,"E7"),sQuery(id+"F0.wireOp",EDGE,"E8"),sQuery(id+"F0.wireOp",EDGE,"E9"),sQuery(id+"F0.wireOp",EDGE,"E10"),sQuery(id+"F0.wireOp",EDGE,"E11"),subQ47,subQ46,subQ45,subQ44,sQuery(id+"F0.wireOp",EDGE,"E16.filletArc"),sQuery(id+"F0.wireOp",EDGE,"E21"),subQ43,sQuery(id+"F0.wireOp",EDGE,"E25"),subQ41,sQuery(id+"F0.wireOp",EDGE,"E29"),subQ39,subQ36,subQ34,subQ33,subQ31,subQ29,subQ26,subQ24,subQ22,subQ20,sQuery(id+"F0.wireOp",EDGE,"E60.filletArc"),sQuery(id+"F0.wireOp",EDGE,"E61.filletArc"),sQuery(id+"F0.wireOp",EDGE,"E62.filletArc")])],"isStart":true}),makeQuery(id+"F2.opExtrude","CAP_FACE",FACE,{"disambiguationData":[OSD([subQ51,subQ50,subQ49,subQ48,subQ47,subQ46,subQ45,subQ44,subQ43,subQ42,subQ41,subQ40,subQ39,subQ38,subQ37,subQ36,subQ35,subQ34,subQ33,subQ32,subQ31,subQ30,subQ29,subQ28,subQ27,subQ26,subQ25,subQ24,subQ23,subQ22,subQ21,subQ20])],"isStart":true})]}),makeQuery(id+"F3.opExtrude","CAP_FACE",FACE,{"disambiguationData":[OSD([subQ19,subQ18,subQ17,subQ16,subQ15,subQ14,subQ13,subQ12,subQ11,subQ10])],"isStart":true}),makeQuery(id+"F3.opExtrude","CAP_FACE",FACE,{"disambiguationData":[OSD([subQ9,subQ8,subQ7,subQ6,subQ5,subQ4,subQ3,subQ2,subQ1,subQ0])],"isStart":true})]});}
            var sketch = newSketch(context, id + "F12", { "sketchPlane" : qUnion([Q0])});
            skCircle(sketch, "E129", {"center": v(55.6, -30.6) * mm, "radius": 3.65 * mm});
            skCircle(sketch, "E130", {"center": v(-31.6, -30.6) * mm, "radius": 3.65 * mm});
            skCircle(sketch, "E131", {"center": v(-31.6, 30.6) * mm, "radius": 3.65 * mm});
            skCircle(sketch, "E132", {"center": v(55.6, 30.6) * mm, "radius": 3.65 * mm});
            skSolve(sketch);
        }
        {
            var Q0;
            Q0=makeQuery(id+"F12.imprint","IMPRINT",FACE,{"disambiguationData":[TD([[makeQuery(id+"F12.imprint","IMPRINT",EDGE,{"derivedFrom":sQuery(id+"F12.wireOp",EDGE,"E129")}),1.0]])]});
            var Q1;
            Q1=makeQuery(id+"F12.imprint","IMPRINT",FACE,{"disambiguationData":[TD([[makeQuery(id+"F12.imprint","IMPRINT",EDGE,{"derivedFrom":sQuery(id+"F12.wireOp",EDGE,"E132")}),1.0]])]});
            var Q2;
            Q2=makeQuery(id+"F12.imprint","IMPRINT",FACE,{"disambiguationData":[TD([[makeQuery(id+"F12.imprint","IMPRINT",EDGE,{"derivedFrom":sQuery(id+"F12.wireOp",EDGE,"E130")}),1.0]])]});
            var Q3;
            Q3=makeQuery(id+"F12.imprint","IMPRINT",FACE,{"disambiguationData":[TD([[makeQuery(id+"F12.imprint","IMPRINT",EDGE,{"derivedFrom":sQuery(id+"F12.wireOp",EDGE,"E131")}),1.0]])]});
            extrude(context, id + "F13", {"entities" : qUnion([Q0, Q1, Q2, Q3]), "operationType" : NewBodyOperationType.REMOVE, "oppositeDirection" : true, "depth" : 3.7 * mm});
        }
        {
            var Q0;
            Q0=makeQuery(id+"F5.opExtrude","CAP_EDGE",EDGE,{"disambiguationData":[OSD([sQuery(id+"F4.wireOp",EDGE,"E74")])],"isStart":true});
            var Q1;
            Q1=makeQuery(id+"F5.opExtrude","CAP_EDGE",EDGE,{"disambiguationData":[OSD([sQuery(id+"F4.wireOp",EDGE,"E125.filletArc")])],"isStart":true});
            var Q2;
            Q2=makeQuery(id+"F5.opExtrude","CAP_EDGE",EDGE,{"disambiguationData":[OSD([sQuery(id+"F4.wireOp",EDGE,"E75")])],"isStart":true});
            var Q3;
            Q3=makeQuery(id+"F5.opExtrude","CAP_EDGE",EDGE,{"disambiguationData":[OSD([sQuery(id+"F4.wireOp",EDGE,"E126.filletArc")])],"isStart":true});
            var Q4;
            Q4=makeQuery(id+"F5.opExtrude","CAP_EDGE",EDGE,{"disambiguationData":[OSD([sQuery(id+"F4.wireOp",EDGE,"E76")])],"isStart":true});
            var Q5;
            Q5=makeQuery(id+"F5.opExtrude","CAP_EDGE",EDGE,{"disambiguationData":[OSD([sQuery(id+"F4.wireOp",EDGE,"E123.filletArc")])],"isStart":true});
            var Q6;
            Q6=makeQuery(id+"F5.opExtrude","CAP_EDGE",EDGE,{"disambiguationData":[OSD([sQuery(id+"F4.wireOp",EDGE,"E73")])],"isStart":true});
            var Q7;
            Q7=makeQuery(id+"F5.opExtrude","CAP_EDGE",EDGE,{"disambiguationData":[OSD([sQuery(id+"F4.wireOp",EDGE,"E124.filletArc")])],"isStart":true});
            fillet(context, id + "F14", {"entities" : qUnion([Q0, Q1, Q2, Q3, Q4, Q5, Q6, Q7]), "radius" : 1 * mm, "tangentPropagation" : true, "allowEdgeOverflow" : false});
        }
        {
            var Q0;
            Q0=makeQuery(id+"F1.opExtrude","CAP_EDGE",EDGE,{"disambiguationData":[OSD([sQuery(id+"F0.wireOp",EDGE,"E61.filletArc")])],"isStart":true});
            fillet(context, id + "F15", {"entities" : qUnion([Q0]), "radius" : 1 * mm, "tangentPropagation" : true, "allowEdgeOverflow" : false});
        }
        {
            var Q0;
            Q0=makeQuery(id+"F6.opExtrude","CAP_FACE",FACE,{"disambiguationData":[OSD([sQuery(id+"F4.wireOp",EDGE,"E69"),sQuery(id+"F4.wireOp",EDGE,"E70"),sQuery(id+"F4.wireOp",EDGE,"E71"),sQuery(id+"F4.wireOp",EDGE,"E72"),sQuery(id+"F4.wireOp",EDGE,"E77"),sQuery(id+"F4.wireOp",EDGE,"E78"),sQuery(id+"F4.wireOp",EDGE,"E79"),sQuery(id+"F4.wireOp",EDGE,"E80"),sQuery(id+"F4.wireOp",EDGE,"E85"),sQuery(id+"F4.wireOp",EDGE,"E86"),sQuery(id+"F4.wireOp",EDGE,"E87"),sQuery(id+"F4.wireOp",EDGE,"E88"),sQuery(id+"F4.wireOp",EDGE,"E89"),sQuery(id+"F4.wireOp",EDGE,"E90"),sQuery(id+"F4.wireOp",EDGE,"E91"),sQuery(id+"F4.wireOp",EDGE,"E92"),sQuery(id+"F4.wireOp",EDGE,"E93"),sQuery(id+"F4.wireOp",EDGE,"E95"),sQuery(id+"F4.wireOp",EDGE,"E97"),sQuery(id+"F4.wireOp",EDGE,"E98"),sQuery(id+"F4.wireOp",EDGE,"E99"),sQuery(id+"F4.wireOp",EDGE,"E100"),sQuery(id+"F4.wireOp",EDGE,"E101"),sQuery(id+"F4.wireOp",EDGE,"E102"),sQuery(id+"F4.wireOp",EDGE,"E103"),sQuery(id+"F4.wireOp",EDGE,"E104"),sQuery(id+"F4.wireOp",EDGE,"E105"),sQuery(id+"F4.wireOp",EDGE,"E106"),sQuery(id+"F4.wireOp",EDGE,"E107"),sQuery(id+"F4.wireOp",EDGE,"E108"),sQuery(id+"F4.wireOp",EDGE,"E112.trimOffspring"),sQuery(id+"F4.wireOp",EDGE,"E114.trimOffspring")])],"isStart":false});
            var sketch = newSketch(context, id + "F16", { "sketchPlane" : qUnion([Q0])});
            skLineSegment(sketch, "E133.0", {"start": v(-36.1, -162) * mm, "end": v(-36.1, -110) * mm});
            skLineSegment(sketch, "E133.1", {"start": v(-31.6, -110) * mm, "end": v(-36.1, -110) * mm});
            skArc(sketch, "E133.2", {"start": v(-31.6, -110) * mm, "mid": v(-28.35, -108.65) * mm, "end": v(-27, -105.4) * mm});
            skLineSegment(sketch, "E133.3", {"start": v(-27, -105.4) * mm, "end": v(-27, -100.9) * mm});
            skLineSegment(sketch, "E133.4", {"start": v(-27, -100.9) * mm, "end": v(51, -100.9) * mm});
            skLineSegment(sketch, "E133.5", {"start": v(51, -105.4) * mm, "end": v(51, -100.9) * mm});
            skArc(sketch, "E133.6", {"start": v(51, -105.4) * mm, "mid": v(52.35, -108.65) * mm, "end": v(55.6, -110) * mm});
            skLineSegment(sketch, "E133.7", {"start": v(55.6, -110) * mm, "end": v(60.1, -110) * mm});
            skLineSegment(sketch, "E133.8", {"start": v(60.1, -110) * mm, "end": v(60.1, -162) * mm});
            skLineSegment(sketch, "E133.9", {"start": v(55.6, -162) * mm, "end": v(60.1, -162) * mm});
            skArc(sketch, "E133.10", {"start": v(55.6, -162) * mm, "mid": v(52.35, -163.35) * mm, "end": v(51, -166.6) * mm});
            skLineSegment(sketch, "E133.11", {"start": v(51, -166.6) * mm, "end": v(51, -171.1) * mm});
            skLineSegment(sketch, "E133.12", {"start": v(51, -171.1) * mm, "end": v(-27, -171.1) * mm});
            skArc(sketch, "E133.13", {"start": v(-27, -166.6) * mm, "mid": v(-28.35, -163.35) * mm, "end": v(-31.6, -162) * mm});
            skLineSegment(sketch, "E133.14", {"start": v(-36.1, -162) * mm, "end": v(-31.6, -162) * mm});
            skLineSegment(sketch, "E133.15", {"start": v(-27, -166.6) * mm, "end": v(-27, -171.1) * mm});
            skLineSegment(sketch, "E134.0", {"start": v(-26.6, -105.4) * mm, "end": v(-26.6, -101.3) * mm});
            skArc(sketch, "E134.1", {"start": v(-31.6, -110.4) * mm, "mid": v(-28.06, -108.94) * mm, "end": v(-26.6, -105.4) * mm});
            skLineSegment(sketch, "E134.2", {"start": v(-31.6, -110.4) * mm, "end": v(-35.7, -110.4) * mm});
            skLineSegment(sketch, "E134.3", {"start": v(-35.7, -161.6) * mm, "end": v(-35.7, -110.4) * mm});
            skLineSegment(sketch, "E134.4", {"start": v(-35.7, -161.6) * mm, "end": v(-31.6, -161.6) * mm});
            skLineSegment(sketch, "E134.5", {"start": v(59.7, -110.4) * mm, "end": v(59.7, -161.6) * mm});
            skLineSegment(sketch, "E134.6", {"start": v(55.6, -110.4) * mm, "end": v(59.7, -110.4) * mm});
            skArc(sketch, "E134.7", {"start": v(50.6, -105.4) * mm, "mid": v(52.06, -108.94) * mm, "end": v(55.6, -110.4) * mm});
            skLineSegment(sketch, "E134.8", {"start": v(50.6, -105.4) * mm, "end": v(50.6, -101.3) * mm});
            skLineSegment(sketch, "E134.9", {"start": v(55.6, -161.6) * mm, "end": v(59.7, -161.6) * mm});
            skArc(sketch, "E134.10", {"start": v(55.6, -161.6) * mm, "mid": v(52.06, -163.06) * mm, "end": v(50.6, -166.6) * mm});
            skLineSegment(sketch, "E134.11", {"start": v(50.6, -166.6) * mm, "end": v(50.6, -170.7) * mm});
            skLineSegment(sketch, "E134.12", {"start": v(50.6, -170.7) * mm, "end": v(-26.6, -170.7) * mm});
            skLineSegment(sketch, "E134.13", {"start": v(-26.6, -166.6) * mm, "end": v(-26.6, -170.7) * mm});
            skLineSegment(sketch, "E134.14", {"start": v(-26.6, -101.3) * mm, "end": v(50.6, -101.3) * mm});
            skArc(sketch, "E134.15", {"start": v(-26.6, -166.6) * mm, "mid": v(-28.06, -163.06) * mm, "end": v(-31.6, -161.6) * mm});
            skLineSegment(sketch, "E135.0", {"start": v(-24.2, -102.8) * mm, "end": v(48.2, -102.8) * mm});
            skArc(sketch, "E135.1", {"start": v(-31.6, -111.8) * mm, "mid": v(-27.07, -109.93) * mm, "end": v(-25.2, -105.4) * mm});
            skLineSegment(sketch, "E135.2", {"start": v(-25.2, -105.4) * mm, "end": v(-25.2, -103.8) * mm});
            skArc(sketch, "E135.3", {"start": v(-25.2, -103.8) * mm, "mid": v(-24.9, -103.1) * mm, "end": v(-24.2, -102.8) * mm});
            skLineSegment(sketch, "E135.4", {"start": v(-31.6, -111.8) * mm, "end": v(-33.2, -111.8) * mm});
            skArc(sketch, "E135.5", {"start": v(-34.2, -112.8) * mm, "mid": v(-33.9, -112.1) * mm, "end": v(-33.2, -111.8) * mm});
            skLineSegment(sketch, "E135.6", {"start": v(-34.2, -159.2) * mm, "end": v(-34.2, -112.8) * mm});
            skArc(sketch, "E135.7", {"start": v(48.2, -102.8) * mm, "mid": v(48.9, -103.1) * mm, "end": v(49.2, -103.8) * mm});
            skLineSegment(sketch, "E135.8", {"start": v(49.2, -105.4) * mm, "end": v(49.2, -103.8) * mm});
            skArc(sketch, "E135.9", {"start": v(49.2, -105.4) * mm, "mid": v(51.07, -109.93) * mm, "end": v(55.6, -111.8) * mm});
            skLineSegment(sketch, "E135.10", {"start": v(55.6, -111.8) * mm, "end": v(57.2, -111.8) * mm});
            skArc(sketch, "E135.11", {"start": v(57.2, -111.8) * mm, "mid": v(57.9, -112.1) * mm, "end": v(58.2, -112.8) * mm});
            skArc(sketch, "E135.12", {"start": v(58.2, -159.2) * mm, "mid": v(57.9, -159.9) * mm, "end": v(57.2, -160.2) * mm});
            skLineSegment(sketch, "E135.13", {"start": v(55.6, -160.2) * mm, "end": v(57.2, -160.2) * mm});
            skArc(sketch, "E135.14", {"start": v(55.6, -160.2) * mm, "mid": v(51.07, -162.07) * mm, "end": v(49.2, -166.6) * mm});
            skArc(sketch, "E135.15", {"start": v(49.2, -168.2) * mm, "mid": v(48.9, -168.9) * mm, "end": v(48.2, -169.2) * mm});
            skLineSegment(sketch, "E135.16", {"start": v(49.2, -166.6) * mm, "end": v(49.2, -168.2) * mm});
            skArc(sketch, "E135.17", {"start": v(-33.2, -160.2) * mm, "mid": v(-33.9, -159.9) * mm, "end": v(-34.2, -159.2) * mm});
            skLineSegment(sketch, "E135.18", {"start": v(-31.6, -160.2) * mm, "end": v(-33.2, -160.2) * mm});
            skArc(sketch, "E135.19", {"start": v(-25.2, -166.6) * mm, "mid": v(-27.07, -162.07) * mm, "end": v(-31.6, -160.2) * mm});
            skLineSegment(sketch, "E135.20", {"start": v(-25.2, -166.6) * mm, "end": v(-25.2, -168.2) * mm});
            skArc(sketch, "E135.21", {"start": v(-24.2, -169.2) * mm, "mid": v(-24.9, -168.9) * mm, "end": v(-25.2, -168.2) * mm});
            skLineSegment(sketch, "E135.22", {"start": v(48.2, -169.2) * mm, "end": v(-24.2, -169.2) * mm});
            skLineSegment(sketch, "E135.23", {"start": v(58.2, -112.8) * mm, "end": v(58.2, -159.2) * mm});
            skArc(sketch, "E136.0", {"start": v(57.2, -111.3) * mm, "mid": v(58.26, -111.74) * mm, "end": v(58.7, -112.8) * mm});
            skLineSegment(sketch, "E136.1", {"start": v(-31.6, -160.7) * mm, "end": v(-33.2, -160.7) * mm});
            skArc(sketch, "E136.2", {"start": v(-25.7, -166.6) * mm, "mid": v(-27.43, -162.43) * mm, "end": v(-31.6, -160.7) * mm});
            skLineSegment(sketch, "E136.3", {"start": v(-25.7, -166.6) * mm, "end": v(-25.7, -168.2) * mm});
            skArc(sketch, "E136.4", {"start": v(-24.2, -169.7) * mm, "mid": v(-25.26, -169.26) * mm, "end": v(-25.7, -168.2) * mm});
            skLineSegment(sketch, "E136.5", {"start": v(48.2, -169.7) * mm, "end": v(-24.2, -169.7) * mm});
            skArc(sketch, "E136.6", {"start": v(49.7, -168.2) * mm, "mid": v(49.26, -169.26) * mm, "end": v(48.2, -169.7) * mm});
            skArc(sketch, "E136.7", {"start": v(58.7, -159.2) * mm, "mid": v(58.26, -160.26) * mm, "end": v(57.2, -160.7) * mm});
            skLineSegment(sketch, "E136.8", {"start": v(55.6, -160.7) * mm, "end": v(57.2, -160.7) * mm});
            skArc(sketch, "E136.9", {"start": v(55.6, -160.7) * mm, "mid": v(51.43, -162.43) * mm, "end": v(49.7, -166.6) * mm});
            skLineSegment(sketch, "E136.10", {"start": v(49.7, -166.6) * mm, "end": v(49.7, -168.2) * mm});
            skArc(sketch, "E136.11", {"start": v(-33.2, -160.7) * mm, "mid": v(-34.26, -160.26) * mm, "end": v(-34.7, -159.2) * mm});
            skLineSegment(sketch, "E136.12", {"start": v(58.7, -112.8) * mm, "end": v(58.7, -159.2) * mm});
            skLineSegment(sketch, "E136.13", {"start": v(-34.7, -159.2) * mm, "end": v(-34.7, -112.8) * mm});
            skArc(sketch, "E136.14", {"start": v(-34.7, -112.8) * mm, "mid": v(-34.26, -111.74) * mm, "end": v(-33.2, -111.3) * mm});
            skLineSegment(sketch, "E136.15", {"start": v(-31.6, -111.3) * mm, "end": v(-33.2, -111.3) * mm});
            skArc(sketch, "E136.16", {"start": v(-31.6, -111.3) * mm, "mid": v(-27.43, -109.57) * mm, "end": v(-25.7, -105.4) * mm});
            skLineSegment(sketch, "E136.17", {"start": v(-25.7, -105.4) * mm, "end": v(-25.7, -103.8) * mm});
            skArc(sketch, "E136.18", {"start": v(-25.7, -103.8) * mm, "mid": v(-25.26, -102.74) * mm, "end": v(-24.2, -102.3) * mm});
            skLineSegment(sketch, "E136.19", {"start": v(-24.2, -102.3) * mm, "end": v(48.2, -102.3) * mm});
            skArc(sketch, "E136.20", {"start": v(48.2, -102.3) * mm, "mid": v(49.26, -102.74) * mm, "end": v(49.7, -103.8) * mm});
            skLineSegment(sketch, "E136.21", {"start": v(49.7, -105.4) * mm, "end": v(49.7, -103.8) * mm});
            skArc(sketch, "E136.22", {"start": v(49.7, -105.4) * mm, "mid": v(51.43, -109.57) * mm, "end": v(55.6, -111.3) * mm});
            skLineSegment(sketch, "E136.23", {"start": v(55.6, -111.3) * mm, "end": v(57.2, -111.3) * mm});
            skSolve(sketch);
        }
        {
            var Q0;
            Q0=makeQuery(id+"F16.imprint","IMPRINT",FACE,{"disambiguationData":[TD([[makeQuery(id+"F16.imprint","IMPRINT",EDGE,{"derivedFrom":sQuery(id+"F16.wireOp",EDGE,"E133.0")}),-1.0]])]});
            var Q1;
            Q1=makeQuery(id+"F5.opExtrude","CAP_FACE",FACE,{"disambiguationData":[OSD([sQuery(id+"F4.wireOp",EDGE,"E73"),sQuery(id+"F4.wireOp",EDGE,"E74"),sQuery(id+"F4.wireOp",EDGE,"E75"),sQuery(id+"F4.wireOp",EDGE,"E76"),sQuery(id+"F4.wireOp",EDGE,"E77"),sQuery(id+"F4.wireOp",EDGE,"E78"),sQuery(id+"F4.wireOp",EDGE,"E79"),sQuery(id+"F4.wireOp",EDGE,"E80"),sQuery(id+"F4.wireOp",EDGE,"E81"),sQuery(id+"F4.wireOp",EDGE,"E82"),sQuery(id+"F4.wireOp",EDGE,"E83"),sQuery(id+"F4.wireOp",EDGE,"E84"),sQuery(id+"F4.wireOp",EDGE,"E85"),sQuery(id+"F4.wireOp",EDGE,"E89"),sQuery(id+"F4.wireOp",EDGE,"E90"),sQuery(id+"F4.wireOp",EDGE,"E91"),sQuery(id+"F4.wireOp",EDGE,"E93"),sQuery(id+"F4.wireOp",EDGE,"E94"),sQuery(id+"F4.wireOp",EDGE,"E95"),sQuery(id+"F4.wireOp",EDGE,"E96"),sQuery(id+"F4.wireOp",EDGE,"E98"),sQuery(id+"F4.wireOp",EDGE,"E100"),sQuery(id+"F4.wireOp",EDGE,"E102"),sQuery(id+"F4.wireOp",EDGE,"E104"),sQuery(id+"F4.wireOp",EDGE,"E106"),sQuery(id+"F4.wireOp",EDGE,"E108"),sQuery(id+"F4.wireOp",EDGE,"E109.trimOffspring"),sQuery(id+"F4.wireOp",EDGE,"E110.trimOffspring"),sQuery(id+"F4.wireOp",EDGE,"E111.trimOffspring"),sQuery(id+"F4.wireOp",EDGE,"E113.trimOffspring"),sQuery(id+"F4.wireOp",EDGE,"E123.filletArc"),sQuery(id+"F4.wireOp",EDGE,"E124.filletArc"),sQuery(id+"F4.wireOp",EDGE,"E125.filletArc"),sQuery(id+"F4.wireOp",EDGE,"E126.filletArc")])],"isStart":false});
            extrude(context, id + "F17", {"entities" : qUnion([Q0]), "operationType" : NewBodyOperationType.REMOVE, "endBound" : BoundingType.UP_TO_SURFACE, "oppositeDirection" : true, "endBoundEntityFace" : qUnion([Q1]), "depth" : 25 * mm});
        }
        {
            var Q0;
            Q0=makeQuery(id+"F16.imprint","IMPRINT",FACE,{"disambiguationData":[TD([[makeQuery(id+"F16.imprint","IMPRINT",EDGE,{"derivedFrom":sQuery(id+"F16.wireOp",EDGE,"E135.0")}),1.0]])]});
            var Q1;
            {var subQ0=sQuery(id+"F4.wireOp",EDGE,"E126.filletArc");var subQ1=sQuery(id+"F4.wireOp",EDGE,"E125.filletArc");var subQ2=sQuery(id+"F4.wireOp",EDGE,"E124.filletArc");var subQ3=sQuery(id+"F4.wireOp",EDGE,"E123.filletArc");var subQ4=sQuery(id+"F4.wireOp",EDGE,"E113.trimOffspring");var subQ5=sQuery(id+"F4.wireOp",EDGE,"E111.trimOffspring");var subQ6=sQuery(id+"F4.wireOp",EDGE,"E110.trimOffspring");var subQ7=sQuery(id+"F4.wireOp",EDGE,"E109.trimOffspring");var subQ8=sQuery(id+"F4.wireOp",EDGE,"E108");var subQ9=sQuery(id+"F4.wireOp",EDGE,"E106");var subQ10=sQuery(id+"F4.wireOp",EDGE,"E104");var subQ11=sQuery(id+"F4.wireOp",EDGE,"E102");var subQ12=sQuery(id+"F4.wireOp",EDGE,"E100");var subQ13=sQuery(id+"F4.wireOp",EDGE,"E98");var subQ14=sQuery(id+"F4.wireOp",EDGE,"E96");var subQ15=sQuery(id+"F4.wireOp",EDGE,"E95");var subQ16=sQuery(id+"F4.wireOp",EDGE,"E94");var subQ17=sQuery(id+"F4.wireOp",EDGE,"E93");var subQ18=sQuery(id+"F4.wireOp",EDGE,"E91");var subQ19=sQuery(id+"F4.wireOp",EDGE,"E90");var subQ20=sQuery(id+"F4.wireOp",EDGE,"E89");var subQ21=sQuery(id+"F4.wireOp",EDGE,"E85");var subQ22=sQuery(id+"F4.wireOp",EDGE,"E84");var subQ23=sQuery(id+"F4.wireOp",EDGE,"E83");var subQ24=sQuery(id+"F4.wireOp",EDGE,"E82");var subQ25=sQuery(id+"F4.wireOp",EDGE,"E81");var subQ26=sQuery(id+"F4.wireOp",EDGE,"E80");var subQ27=sQuery(id+"F4.wireOp",EDGE,"E79");var subQ28=sQuery(id+"F4.wireOp",EDGE,"E78");var subQ29=sQuery(id+"F4.wireOp",EDGE,"E77");var subQ30=sQuery(id+"F4.wireOp",EDGE,"E76");var subQ31=sQuery(id+"F4.wireOp",EDGE,"E75");var subQ32=sQuery(id+"F4.wireOp",EDGE,"E74");var subQ33=sQuery(id+"F4.wireOp",EDGE,"E73");Q1=makeQuery(id+"F17.boolean.opBoolean","MERGE",FACE,{"derivedFrom":[makeQuery(id+"F5.opExtrude","CAP_FACE",FACE,{"disambiguationData":[OSD([subQ33,subQ32,subQ31,subQ30,subQ29,subQ28,subQ27,subQ26,subQ25,subQ24,subQ23,subQ22,subQ21,subQ20,subQ19,subQ18,subQ17,subQ16,subQ15,subQ14,subQ13,subQ12,subQ11,subQ10,subQ9,subQ8,subQ7,subQ6,subQ5,subQ4,subQ3,subQ2,subQ1,subQ0])],"isStart":false}),makeQuery(id+"F17.opExtrude","CAP_FACE",FACE,{"disambiguationData":[OSD([subQ33,subQ32,subQ31,subQ30,subQ29,subQ28,subQ27,subQ26,subQ25,subQ24,subQ23,subQ22,subQ21,subQ20,subQ19,subQ18,subQ17,subQ16,subQ15,subQ14,subQ13,subQ12,subQ11,subQ10,subQ9,subQ8,subQ7,subQ6,subQ5,subQ4,subQ3,subQ2,subQ1,subQ0])],"isStart":false})]});}
            extrude(context, id + "F18", {"entities" : qUnion([Q0]), "operationType" : NewBodyOperationType.REMOVE, "endBound" : BoundingType.UP_TO_SURFACE, "oppositeDirection" : true, "endBoundEntityFace" : qUnion([Q1]), "depth" : 25 * mm});
        }
        {
            var Q0;
            Q0=makeQuery(id+"F17.boolean.opBoolean","COPY",EDGE,{"derivedFrom":makeQuery(id+"F17.opExtrude","SWEPT_EDGE",EDGE,{"disambiguationData":[OSD([sQuery(id+"F16.wireOp",EDGE,"E134.5"),sQuery(id+"F16.wireOp",EDGE,"E134.9")])]})});
            var Q1;
            Q1=makeQuery(id+"F17.boolean.opBoolean","COPY",EDGE,{"derivedFrom":makeQuery(id+"F17.opExtrude","SWEPT_EDGE",EDGE,{"disambiguationData":[OSD([sQuery(id+"F16.wireOp",EDGE,"E134.11"),sQuery(id+"F16.wireOp",EDGE,"E134.12")])]})});
            var Q2;
            Q2=makeQuery(id+"F17.boolean.opBoolean","COPY",EDGE,{"derivedFrom":makeQuery(id+"F17.opExtrude","SWEPT_EDGE",EDGE,{"disambiguationData":[OSD([sQuery(id+"F16.wireOp",EDGE,"E134.12"),sQuery(id+"F16.wireOp",EDGE,"E134.13")])]})});
            var Q3;
            Q3=makeQuery(id+"F17.boolean.opBoolean","COPY",EDGE,{"derivedFrom":makeQuery(id+"F17.opExtrude","SWEPT_EDGE",EDGE,{"disambiguationData":[OSD([sQuery(id+"F16.wireOp",EDGE,"E134.3"),sQuery(id+"F16.wireOp",EDGE,"E134.4")])]})});
            var Q4;
            Q4=makeQuery(id+"F17.boolean.opBoolean","COPY",EDGE,{"derivedFrom":makeQuery(id+"F17.opExtrude","SWEPT_EDGE",EDGE,{"disambiguationData":[OSD([sQuery(id+"F16.wireOp",EDGE,"E134.2"),sQuery(id+"F16.wireOp",EDGE,"E134.3")])]})});
            var Q5;
            Q5=makeQuery(id+"F17.boolean.opBoolean","COPY",EDGE,{"derivedFrom":makeQuery(id+"F17.opExtrude","SWEPT_EDGE",EDGE,{"disambiguationData":[OSD([sQuery(id+"F16.wireOp",EDGE,"E134.0"),sQuery(id+"F16.wireOp",EDGE,"E134.14")])]})});
            var Q6;
            Q6=makeQuery(id+"F17.boolean.opBoolean","COPY",EDGE,{"derivedFrom":makeQuery(id+"F17.opExtrude","SWEPT_EDGE",EDGE,{"disambiguationData":[OSD([sQuery(id+"F16.wireOp",EDGE,"E134.8"),sQuery(id+"F16.wireOp",EDGE,"E134.14")])]})});
            var Q7;
            Q7=makeQuery(id+"F17.boolean.opBoolean","COPY",EDGE,{"derivedFrom":makeQuery(id+"F17.opExtrude","SWEPT_EDGE",EDGE,{"disambiguationData":[OSD([sQuery(id+"F16.wireOp",EDGE,"E134.5"),sQuery(id+"F16.wireOp",EDGE,"E134.6")])]})});
            fillet(context, id + "F19", {"entities" : qUnion([Q0, Q1, Q2, Q3, Q4, Q5, Q6, Q7]), "radius" : 2 * mm, "tangentPropagation" : true, "allowEdgeOverflow" : false});
        }
        {
            var Q0;
            Q0=makeQuery(id+"F6.opExtrude","CAP_FACE",FACE,{"disambiguationData":[OSD([sQuery(id+"F4.wireOp",EDGE,"E69"),sQuery(id+"F4.wireOp",EDGE,"E70"),sQuery(id+"F4.wireOp",EDGE,"E71"),sQuery(id+"F4.wireOp",EDGE,"E72"),sQuery(id+"F4.wireOp",EDGE,"E77"),sQuery(id+"F4.wireOp",EDGE,"E78"),sQuery(id+"F4.wireOp",EDGE,"E79"),sQuery(id+"F4.wireOp",EDGE,"E80"),sQuery(id+"F4.wireOp",EDGE,"E85"),sQuery(id+"F4.wireOp",EDGE,"E86"),sQuery(id+"F4.wireOp",EDGE,"E87"),sQuery(id+"F4.wireOp",EDGE,"E88"),sQuery(id+"F4.wireOp",EDGE,"E89"),sQuery(id+"F4.wireOp",EDGE,"E90"),sQuery(id+"F4.wireOp",EDGE,"E91"),sQuery(id+"F4.wireOp",EDGE,"E92"),sQuery(id+"F4.wireOp",EDGE,"E93"),sQuery(id+"F4.wireOp",EDGE,"E95"),sQuery(id+"F4.wireOp",EDGE,"E97"),sQuery(id+"F4.wireOp",EDGE,"E98"),sQuery(id+"F4.wireOp",EDGE,"E99"),sQuery(id+"F4.wireOp",EDGE,"E100"),sQuery(id+"F4.wireOp",EDGE,"E101"),sQuery(id+"F4.wireOp",EDGE,"E102"),sQuery(id+"F4.wireOp",EDGE,"E103"),sQuery(id+"F4.wireOp",EDGE,"E104"),sQuery(id+"F4.wireOp",EDGE,"E105"),sQuery(id+"F4.wireOp",EDGE,"E106"),sQuery(id+"F4.wireOp",EDGE,"E107"),sQuery(id+"F4.wireOp",EDGE,"E108"),sQuery(id+"F4.wireOp",EDGE,"E112.trimOffspring"),sQuery(id+"F4.wireOp",EDGE,"E114.trimOffspring")])],"isStart":false});
            var sketch = newSketch(context, id + "F20", { "sketchPlane" : qUnion([Q0])});
            skLineSegment(sketch, "E137.0", {"start": v(-24.6, -101.3) * mm, "end": v(48.6, -101.3) * mm});
            skLineSegment(sketch, "E137.1", {"start": v(-24.2, -102.3) * mm, "end": v(48.2, -102.3) * mm});
            skSolve(sketch);
        }
        {
            var Q0;
            Q0=makeQuery(id+"F20.imprint","IMPRINT",FACE,{"disambiguationData":[TD([[makeQuery(id+"F20.imprint","IMPRINT",EDGE,{"derivedFrom":sQuery(id+"F20.wireOp",EDGE,"E137.1")}),-1.0]])]});
            var sketch = newSketch(context, id + "F21", { "sketchPlane" : qUnion([Q0])});
            skSolve(sketch);
        }
        {
            var Q0;
            Q0=makeQuery(id+"F21.imprint","IMPRINT",FACE,{"disambiguationData":[TD([[makeQuery(id+"F21.imprint","IMPRINT",EDGE,{"derivedFrom":makeQuery(id+"F20.imprint","IMPRINT",EDGE,{"derivedFrom":sQuery(id+"F20.wireOp",EDGE,"E137.1")})}),-1.0]])]});
            var sketch = newSketch(context, id + "F22", { "sketchPlane" : qUnion([Q0])});
            skSolve(sketch);
        }
        {
            var Q0;
            Q0=makeQuery(id+"F1.opExtrude","SWEPT_BODY",BODY,{"disambiguationData":[OSD([sQuery(id+"F0.wireOp",EDGE,"E1"),sQuery(id+"F0.wireOp",EDGE,"E2"),sQuery(id+"F0.wireOp",EDGE,"E3"),sQuery(id+"F0.wireOp",EDGE,"E6"),sQuery(id+"F0.wireOp",EDGE,"E12.bottom"),sQuery(id+"F0.wireOp",EDGE,"E12.top"),sQuery(id+"F0.wireOp",EDGE,"E12.left"),sQuery(id+"F0.wireOp",EDGE,"E12.right"),sQuery(id+"F0.wireOp",EDGE,"E17"),sQuery(id+"F0.wireOp",EDGE,"E18.MirrorCS"),sQuery(id+"F0.wireOp",EDGE,"E19.trimOffspring"),sQuery(id+"F0.wireOp",EDGE,"E20.trimOffspring"),sQuery(id+"F0.wireOp",EDGE,"E23"),sQuery(id+"F0.wireOp",EDGE,"E24"),sQuery(id+"F0.wireOp",EDGE,"E27"),sQuery(id+"F0.wireOp",EDGE,"E28"),sQuery(id+"F0.wireOp",EDGE,"E31"),sQuery(id+"F0.wireOp",EDGE,"E32"),sQuery(id+"F0.wireOp",EDGE,"E33"),sQuery(id+"F0.wireOp",EDGE,"E34"),sQuery(id+"F0.wireOp",EDGE,"E36"),sQuery(id+"F0.wireOp",EDGE,"E37"),sQuery(id+"F0.wireOp",EDGE,"E39"),sQuery(id+"F0.wireOp",EDGE,"E41"),sQuery(id+"F0.wireOp",EDGE,"E42"),sQuery(id+"F0.wireOp",EDGE,"E44"),sQuery(id+"F0.wireOp",EDGE,"E46"),sQuery(id+"F0.wireOp",EDGE,"E47"),sQuery(id+"F0.wireOp",EDGE,"E48"),sQuery(id+"F0.wireOp",EDGE,"E49"),sQuery(id+"F0.wireOp",EDGE,"E51"),sQuery(id+"F0.wireOp",EDGE,"E52"),sQuery(id+"F0.wireOp",EDGE,"E54"),sQuery(id+"F0.wireOp",EDGE,"E55"),sQuery(id+"F0.wireOp",EDGE,"E57"),sQuery(id+"F0.wireOp",EDGE,"E58")])]});
            var Q1;
            Q1=qCreatedBy(makeId("Right.planeOp"),FACE);
            transform(context, id + "F23", {"entities" : qUnion([Q0]), "transformType" : TransformType.TRANSLATION_DISTANCE, "transformDirection" : qUnion([Q1]), "distance" : 152.4 * mm, "makeCopy" : true});
        }
    });
